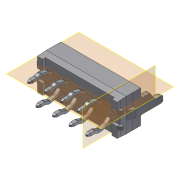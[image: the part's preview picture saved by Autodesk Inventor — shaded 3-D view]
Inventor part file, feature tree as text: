
AUTODESK INVENTOR PART (.ipt)
format: ipt  version: 2014 (Build 180170000, 170)  size: 850,432 bytes
history: native  units: mm
features: plane x2, other x1
ambient origin geometry x8: Origin, YZ Plane, XZ Plane, XY Plane, X Axis, Y Axis, Z Axis, Center Point
bodies: Volumenkörper1 (feature_tree)
feature tree (3):
  other  "micro-miniature_steckverbinder_a-30-08p-1300"
  plane  "Arbeitsebene4"
  plane  "Arbeitsebene5"
